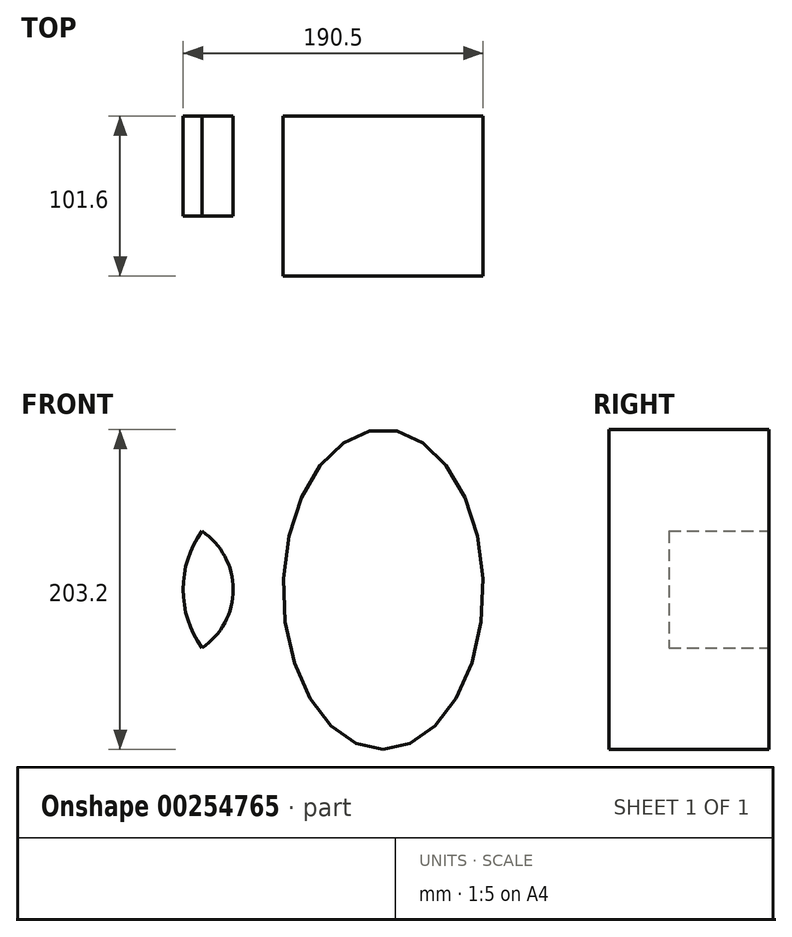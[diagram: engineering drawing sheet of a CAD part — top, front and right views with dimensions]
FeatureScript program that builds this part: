
annotation { "Feature Type Name" : "Feature", "Feature Type Description" : "" }
export const myFeature = defineFeature(function(context is Context, id is Id, definition is map)
    precondition{}
    {
        {
            var Q0;
            Q0=qCreatedBy(makeId("Front.planeOp"),FACE);
            var sketch = newSketch(context, id + "F0", { "sketchPlane" : qUnion([Q0])});
            skLineSegment(sketch, "E0", {"start": v(0, 0) * mm, "end": v(-76.2, 0) * mm});
            skCircle(sketch, "E1", {"center": v(-76.2, 0) * mm, "radius": 44.45 * mm});
            skLineSegment(sketch, "E2", {"start": v(-31.75, 0) * mm, "end": v(-63.5, 0) * mm});
            skCircle(sketch, "E3", {"center": v(0, 0) * mm, "radius": 63.5 * mm});
            skLineSegment(sketch, "E4", {"start": v(63.5, 0) * mm, "end": v(63.5, 101.6) * mm});
            skEllipse(sketch, "E5", {"center": v(63.5, 0) * mm, "majorRadius": 63.5 * mm, "minorRadius": 101.6 * mm, "majorAxis": v(-1, 0)});
            skSolve(sketch);
        }
        {
            var Q0;
            {var subQ0=sQuery(id+"F0.wireOp",EDGE,"E3");var subQ1=sQuery(id+"F0.wireOp",EDGE,"E1");var subQ2=makeQuery(id+"F0.imprint","INTERSECT",VERTEX,{"disambiguationData":[OD(0.0)],"derivedFrom":[subQ1,subQ0]});Q0=makeQuery(id+"F0.imprint","IMPRINT",FACE,{"disambiguationData":[TD([[makeQuery(id+"F0.imprint","IMPRINT",EDGE,{"disambiguationData":[TD([[subQ2,-1.0]])],"derivedFrom":subQ1}),1.0]])]});}
            extrude(context, id + "F1", {"entities" : qUnion([Q0]), "depth" : 25.4 * mm});
        }
        {
            var Q0;
            {var subQ0=sQuery(id+"F0.wireOp",EDGE,"E2");Q0=makeQuery(id+"F0.imprint","IMPRINT",FACE,{"disambiguationData":[TD([[makeQuery(id+"F0.imprint","IMPRINT",EDGE,{"derivedFrom":subQ0}),-1.0]])]});}
            var Q1;
            {var subQ0=sQuery(id+"F0.wireOp",EDGE,"E2");Q1=makeQuery(id+"F0.imprint","IMPRINT",FACE,{"disambiguationData":[TD([[makeQuery(id+"F0.imprint","IMPRINT",EDGE,{"derivedFrom":subQ0}),1.0]])]});}
            var Q2;
            {var subQ3=sQuery(id+"F0.wireOp",EDGE,"E1");var subQ5=sQuery(id+"F0.wireOp",EDGE,"E3");var subQ6=makeQuery(id+"F0.imprint","INTERSECT",VERTEX,{"disambiguationData":[OD(0.0)],"derivedFrom":[subQ3,subQ5]});Q2=makeQuery(id+"F0.imprint","IMPRINT",FACE,{"disambiguationData":[TD([[makeQuery(id+"F0.imprint","IMPRINT",EDGE,{"disambiguationData":[TD([[subQ6,1.0]])],"derivedFrom":subQ5}),1.0]])]});}
            var Q3;
            {var subQ3=sQuery(id+"F0.wireOp",EDGE,"E1");var subQ5=sQuery(id+"F0.wireOp",EDGE,"E3");var subQ6=makeQuery(id+"F0.imprint","INTERSECT",VERTEX,{"disambiguationData":[OD(1.0)],"derivedFrom":[subQ3,subQ5]});Q3=makeQuery(id+"F0.imprint","IMPRINT",FACE,{"disambiguationData":[TD([[makeQuery(id+"F0.imprint","IMPRINT",EDGE,{"disambiguationData":[TD([[subQ6,-1.0]])],"derivedFrom":subQ5}),1.0]])]});}
            extrude(context, id + "F2", {"entities" : qUnion([Q0, Q1, Q2, Q3]), "operationType" : NewBodyOperationType.ADD, "depth" : 63.5 * mm});
        }
        {
            var Q0;
            {var subQ0=sQuery(id+"F0.wireOp",EDGE,"E3");var subQ1=makeQuery(id+"F0.imprint","INTERSECT",VERTEX,{"derivedFrom":[subQ0,sQuery(id+"F0.wireOp",EDGE,"E4")]});Q0=makeQuery(id+"F0.imprint","IMPRINT",FACE,{"disambiguationData":[TD([[makeQuery(id+"F0.imprint","IMPRINT",EDGE,{"disambiguationData":[TD([[subQ1,-1.0]])],"derivedFrom":subQ0}),1.0]])]});}
            var Q1;
            {var subQ0=sQuery(id+"F0.wireOp",EDGE,"E4");Q1=makeQuery(id+"F0.imprint","IMPRINT",FACE,{"disambiguationData":[TD([[makeQuery(id+"F0.imprint","IMPRINT",EDGE,{"derivedFrom":subQ0}),-1.0]])]});}
            var Q2;
            {var subQ0=sQuery(id+"F0.wireOp",EDGE,"E4");Q2=makeQuery(id+"F0.imprint","IMPRINT",FACE,{"disambiguationData":[TD([[makeQuery(id+"F0.imprint","IMPRINT",EDGE,{"derivedFrom":subQ0}),1.0]])]});}
            extrude(context, id + "F3", {"entities" : qUnion([Q0, Q1, Q2]), "operationType" : NewBodyOperationType.ADD, "depth" : 101.6 * mm});
        }
    });
